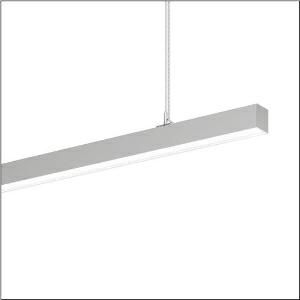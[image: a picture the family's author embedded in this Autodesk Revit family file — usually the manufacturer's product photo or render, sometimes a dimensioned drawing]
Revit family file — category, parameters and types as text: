
# Revit family: silica_r__21_51mx30da44sb_e9ec
name_source: partatom
category: Lighting Fixtures
units: mm (PartAtom-declared; Revit-internal decimal feet)

## family parameters
Cut with Voids When Loaded = No
Host = Face
Light Source = No
Part Type = Normal
Room Calculation Point = No
Round Connector Dimension = Use Diameter
Shared = No

## types (1)
- --- (1 x LED, 4210 lm, 26 W, 4000K)
    Apparent Load = 26 VA
    CIE Flux Codes = 47 79 96 57 100
    Color Rendering = 80
    Color Temperature = 4000K
    Default Elevation = 1800 mm
    Description = Silica® 21, office luminaire, primary optical cover: cover, of PMMA, opal, light emission: direct/indirect distribution, primary light characteristic: symmetric, installation type: suspended mounting, LED, rated luminous flux: 4.210lm, luminous efficacy: 162lm/W, light colour: 840, colour temperature: 4000K, with terminal, 3+2-pole, max. 2.5mm², mains connection: 220..240V, AC, 50/60Hz, rated input power: 26W, luminaire housing, of aluminium, metallic grey (RAL 9006), length: 1.204mm, width: 53mm, height: 53mm, protection rating (complete): IP20, insulation class (complete): insulation class I (protective earthing), certification: CE, permissible operating ambient temperature: 0..+35°C, standard: EN 50419, packaging unit: 1 piece
    Height = 53 mm
    Lamp = 1 x LED
    Lamp Light Flux = 4210 lm
    Lamp Power = 26 W
    Lamp count = 1
    Length = 1204 mm
    Luminous efficacy = 162 lm/W
    Manufacturer = Siteco
    ModVariant = No
    Model = 51MX30DA44SB
    Mounting Place = Ceiling
    Mounting Type = Pendant
    Number of Poles = 1
    OnlyDefault = Yes
    Power Factor = 1
    Product Name = Silica® 21
    Product group = office luminaire | ceiling pendant
    ProductGroupID = 902
    Protection Class = Protection class I
    Protection Degree = IP 20
    RLX_Detail_Level = 1
    RLX_Emergency_Light_Flux = 0 lm
    RLX_Emergency_Type = 0
    RLX_Emergency_Type_DB = No
    RlxData = <blob elided: 23161 chars, md5=d455e766>
    Socket = socket
    Standby Power = 0 W
    System Light Flux = 4210 lm
    System Power = 26 W
    Type Comments = factory setting: luminous flux: 100 % | dim-lin: 254 | 218 mA
    Type Image = l_1297747.jpg
    URL = http://relux.com
    VarID = @adj_047225
    Voltage = 0 V
    Weight = 0.00 kg
    Width = 53 mm

## geometry (parser evidence)
native form markers: Blend x4, Sweep x12
no freeform markers — native parametric forms only
